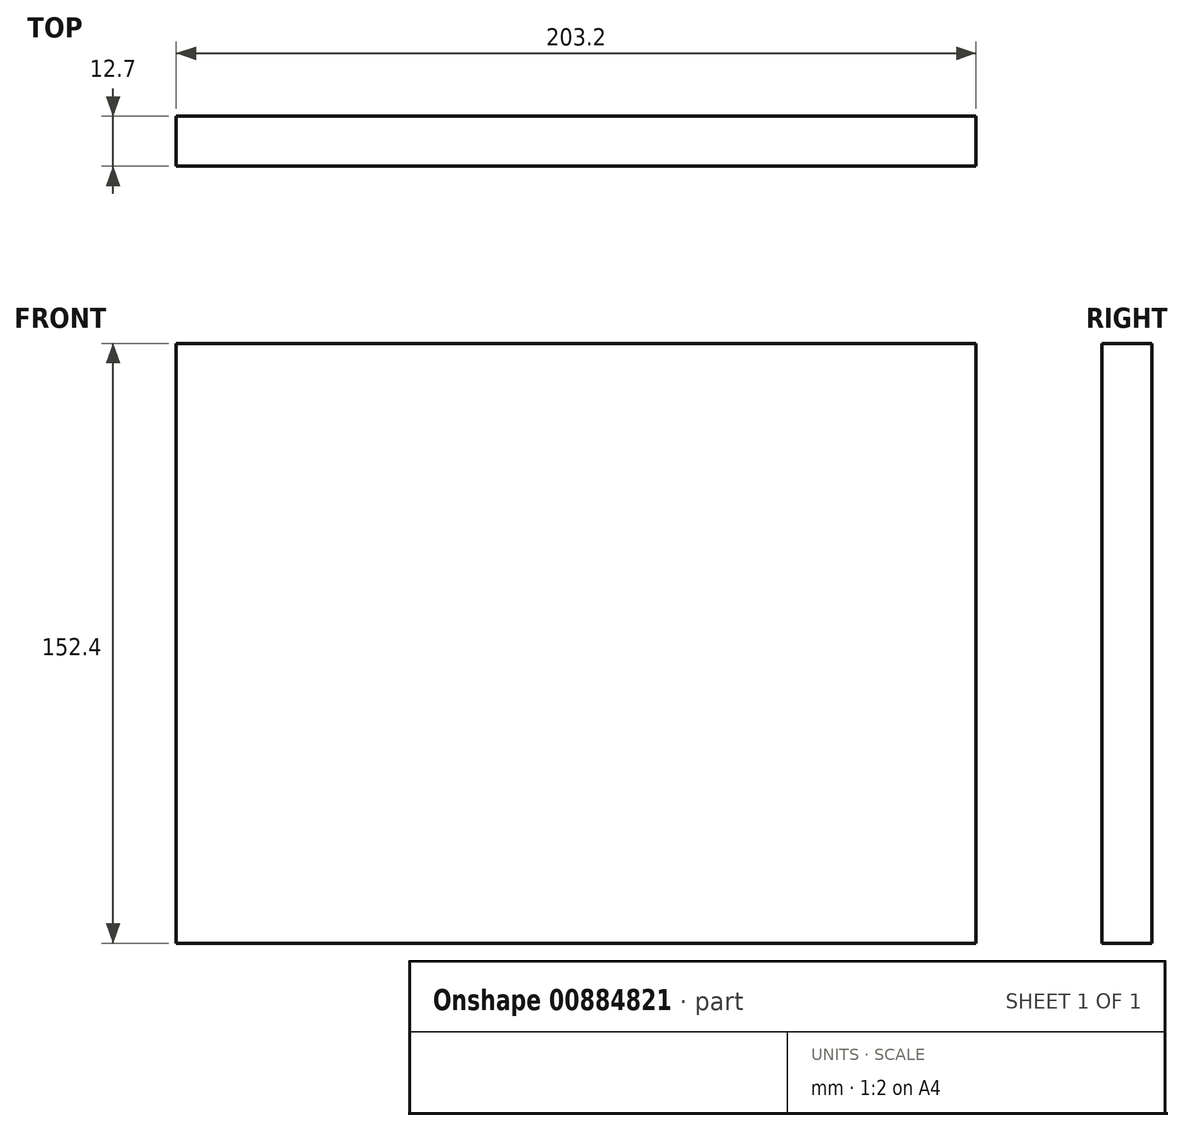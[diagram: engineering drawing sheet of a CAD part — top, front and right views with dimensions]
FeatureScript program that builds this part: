
annotation { "Feature Type Name" : "Feature", "Feature Type Description" : "" }
export const myFeature = defineFeature(function(context is Context, id is Id, definition is map)
    precondition{}
    {
        {
            var Q0;
            Q0=qCreatedBy(makeId("Front.planeOp"),FACE);
            var sketch = newSketch(context, id + "F0", { "sketchPlane" : qUnion([Q0])});
            skLineSegment(sketch, "E0.bottom", {"start": v(101.6, 76.2) * mm, "end": v(-101.6, 76.2) * mm});
            skLineSegment(sketch, "E0.top", {"start": v(101.6, -76.2) * mm, "end": v(-101.6, -76.2) * mm});
            skLineSegment(sketch, "E0.left", {"start": v(101.6, 76.2) * mm, "end": v(101.6, -76.2) * mm});
            skLineSegment(sketch, "E0.right", {"start": v(-101.6, 76.2) * mm, "end": v(-101.6, -76.2) * mm});
            skPoint(sketch, "E0.middle", {"position": v(0, 0) * mm});
            skSolve(sketch);
        }
        {
            var Q0;
            Q0 = qSketchRegion(id + "F0", true);
            extrude(context, id + "F1", {"entities" : qUnion([Q0]), "endBound" : BoundingType.SYMMETRIC, "depth" : 12.7 * mm, "offsetDistance" : 25.4 * mm});
        }
    });
